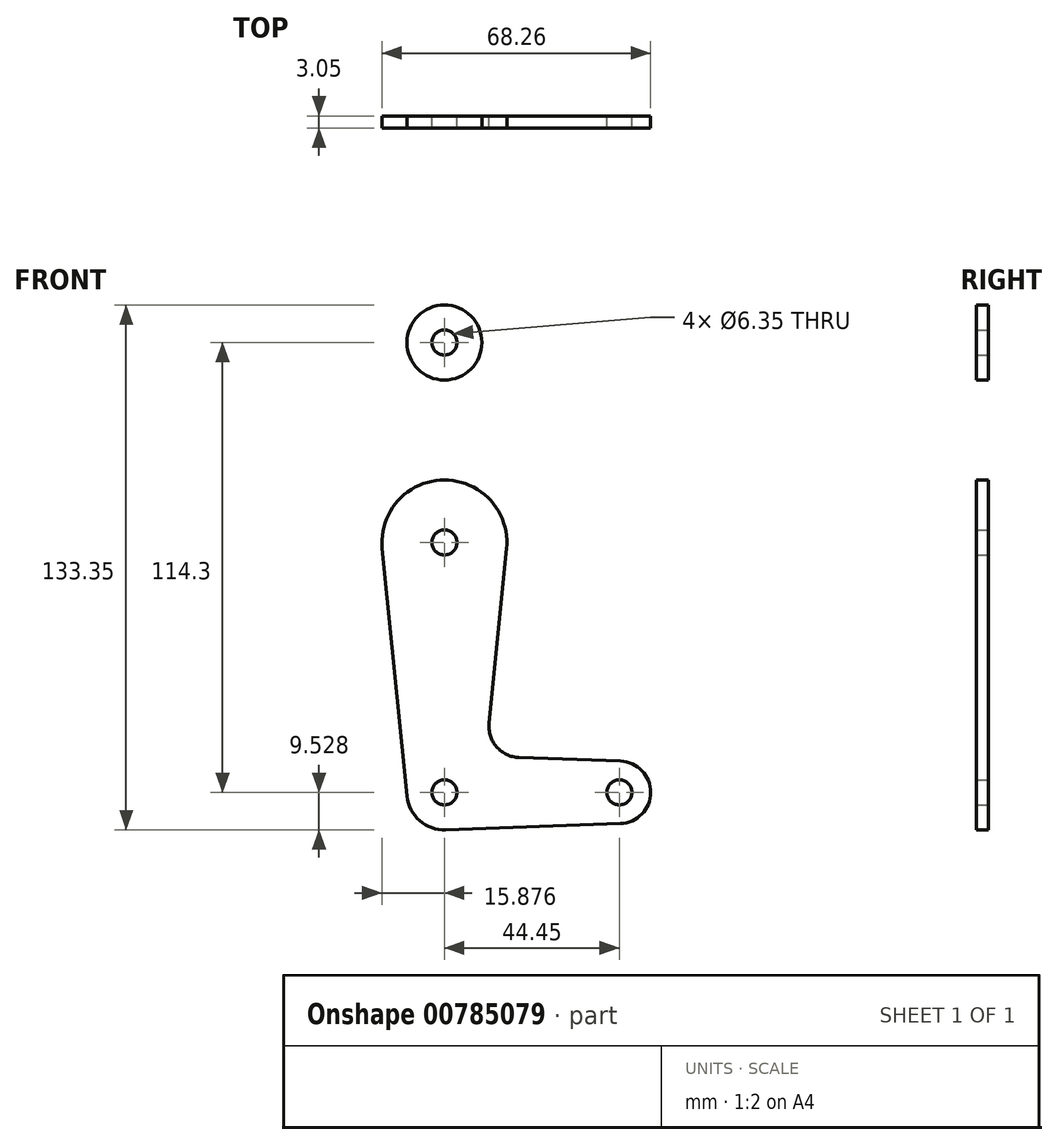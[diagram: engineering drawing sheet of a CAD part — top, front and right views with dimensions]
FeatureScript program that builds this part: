
annotation { "Feature Type Name" : "Feature", "Feature Type Description" : "" }
export const myFeature = defineFeature(function(context is Context, id is Id, definition is map)
    precondition{}
    {
        {
            var Q0;
            Q0=qCreatedBy(makeId("Front.planeOp"),FACE);
            var sketch = newSketch(context, id + "F0", { "sketchPlane" : qUnion([Q0])});
            skLineSegment(sketch, "E0", {"start": v(-38.43, 68.88) * mm, "end": v(-38.43, -45.42) * mm, "construction": true});
            skLineSegment(sketch, "E1", {"start": v(-38.43, -45.42) * mm, "end": v(6.02, -45.42) * mm, "construction": true});
            skCircle(sketch, "E2", {"center": v(-38.43, 68.88) * mm, "radius": 9.53 * mm});
            skCircle(sketch, "E3", {"center": v(-38.43, 18.08) * mm, "radius": 15.88 * mm});
            skCircle(sketch, "E4", {"center": v(-38.43, -45.42) * mm, "radius": 9.53 * mm});
            skCircle(sketch, "E5", {"center": v(6.02, -45.42) * mm, "radius": 7.94 * mm});
            skLineSegment(sketch, "E6", {"start": v(-47.88, 70.07) * mm, "end": v(-54.18, 20.06) * mm});
            skLineSegment(sketch, "E7", {"start": v(-22.68, 20.06) * mm, "end": v(-28.83, 68.88) * mm});
            skLineSegment(sketch, "E8", {"start": v(-54.23, 16.5) * mm, "end": v(-47.91, -46.37) * mm});
            skLineSegment(sketch, "E9", {"start": v(-22.64, 16.5) * mm, "end": v(-27.1, -27.83) * mm});
            skLineSegment(sketch, "E10", {"start": v(-19.47, -36.57) * mm, "end": v(6.3, -37.5) * mm});
            skLineSegment(sketch, "E11", {"start": v(6.3, -53.35) * mm, "end": v(-38.1, -54.94) * mm});
            skCircle(sketch, "E12", {"center": v(-38.43, 68.88) * mm, "radius": 3.18 * mm});
            skCircle(sketch, "E13", {"center": v(-38.43, 18.08) * mm, "radius": 3.18 * mm});
            skCircle(sketch, "E14", {"center": v(-38.43, -45.42) * mm, "radius": 3.18 * mm});
            skCircle(sketch, "E15", {"center": v(6.02, -45.42) * mm, "radius": 3.18 * mm});
            skArc(sketch, "E16.filletArc", {"start": v(-27.1, -27.83) * mm, "mid": v(-25.17, -33.86) * mm, "end": v(-19.47, -36.57) * mm});
            skSolve(sketch);
        }
        {
            var Q0;
            Q0 = qSketchRegion(id + "F0", true);
            extrude(context, id + "F1", {"entities" : qUnion([Q0]), "depth" : 3.05 * mm, "offsetDistance" : 25.4 * mm});
        }
    });
